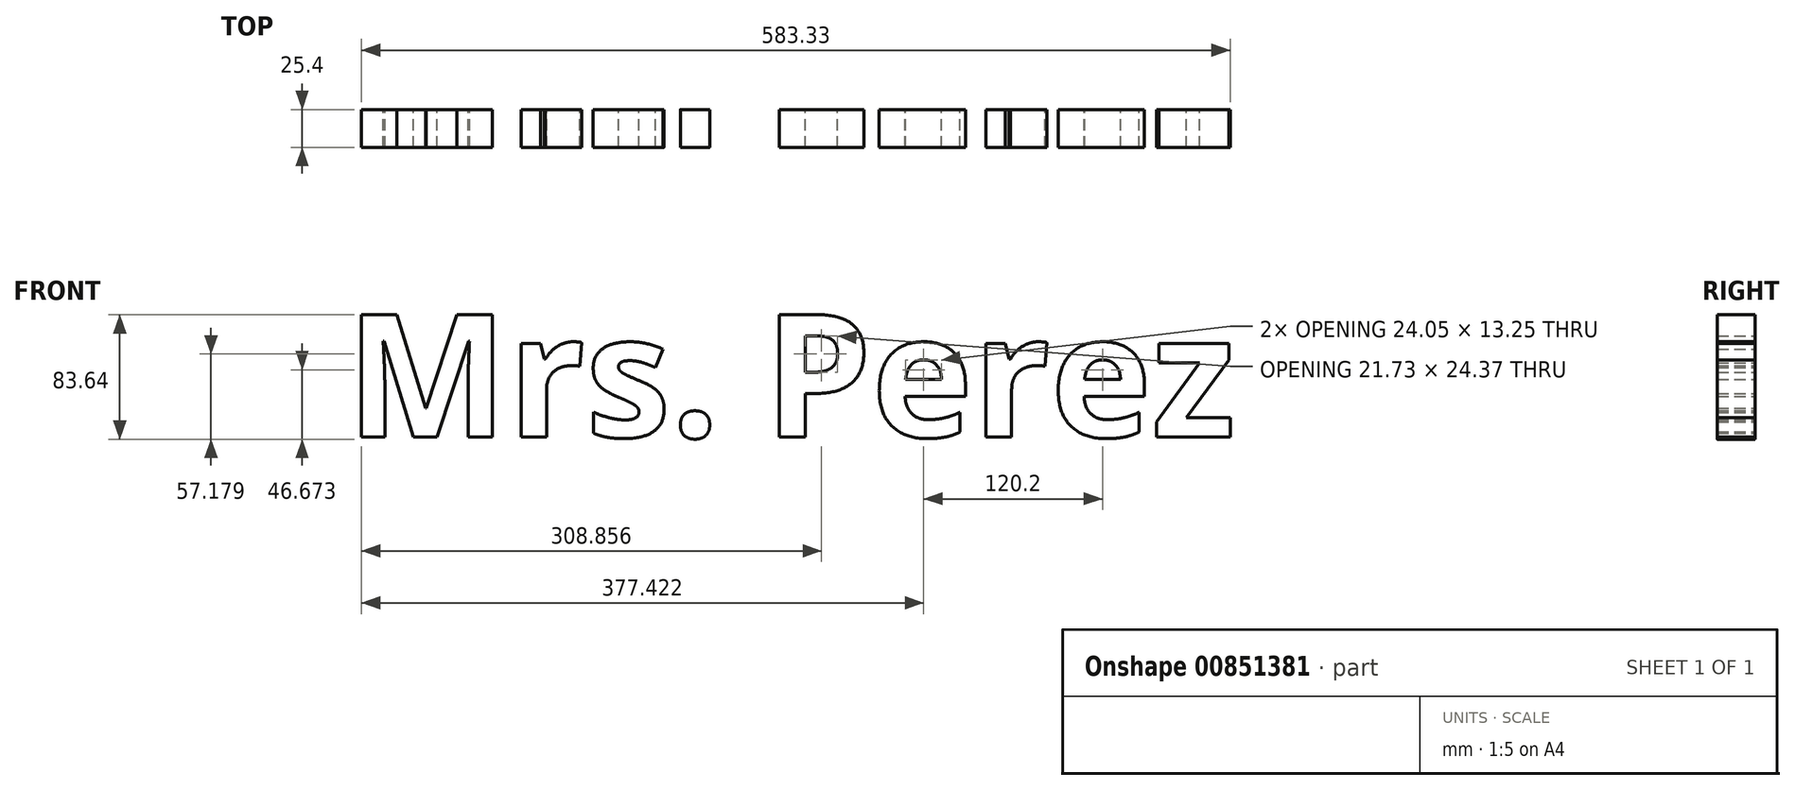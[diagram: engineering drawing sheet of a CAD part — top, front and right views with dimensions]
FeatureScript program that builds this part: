
annotation { "Feature Type Name" : "Feature", "Feature Type Description" : "" }
export const myFeature = defineFeature(function(context is Context, id is Id, definition is map)
    precondition{}
    {
        {
            var Q0;
            Q0=qCreatedBy(makeId("Front.planeOp"),FACE);
            var sketch = newSketch(context, id + "F0", { "sketchPlane" : qUnion([Q0])});
            skText(sketch, "E0", { "text": "Mrs. Perez", "fontName": "OpenSans-Bold.ttf"});
            const initialGuessF0  = {"E0": [-0.08034, -0.04108, 1, 0, 0.08283]};
            skSetInitialGuess(sketch, initialGuessF0);
            skSolve(sketch);
        }
        {
            var Q0;
            Q0 = qSketchRegion(id + "F0", true);
            extrude(context, id + "F1", {"entities" : qUnion([Q0]), "depth" : 25.4 * mm, "offsetDistance" : 25.4 * mm});
        }
    });
